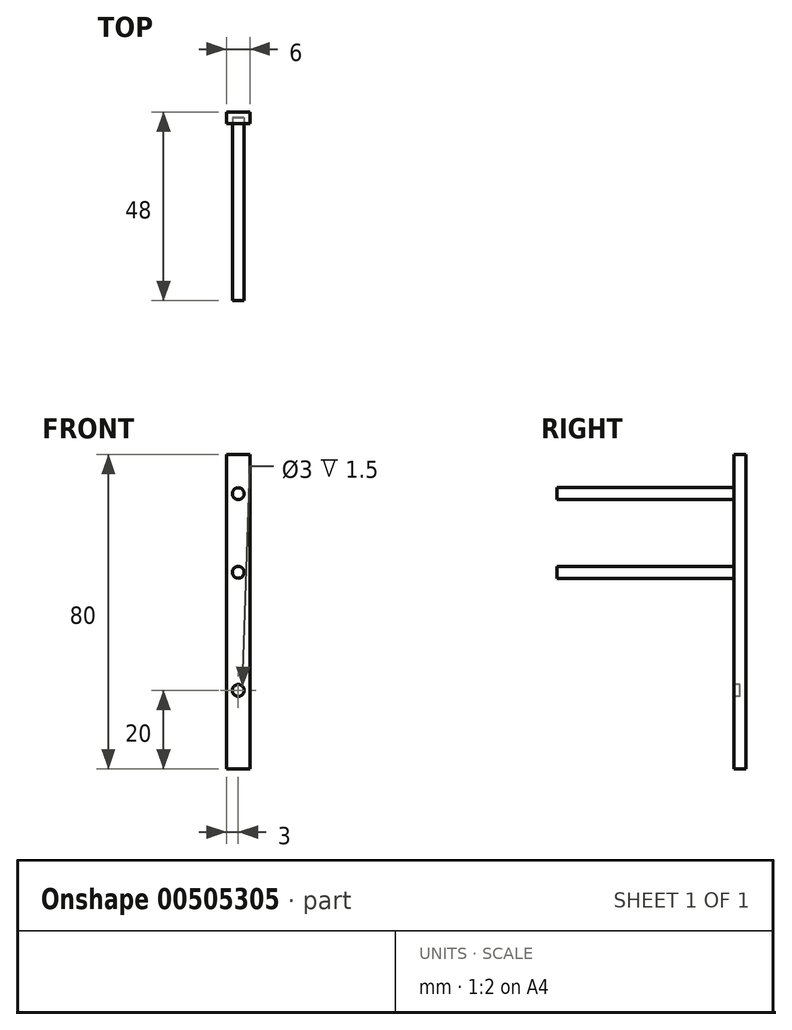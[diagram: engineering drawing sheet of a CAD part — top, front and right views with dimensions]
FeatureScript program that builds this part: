
annotation { "Feature Type Name" : "Feature", "Feature Type Description" : "" }
export const myFeature = defineFeature(function(context is Context, id is Id, definition is map)
    precondition{}
    {
        {
            var Q0;
            Q0=qCreatedBy(makeId("Front.planeOp"),FACE);
            var sketch = newSketch(context, id + "F0", { "sketchPlane" : qUnion([Q0])});
            skLineSegment(sketch, "E0.bottom", {"start": v(3, 40) * mm, "end": v(-3, 40) * mm});
            skLineSegment(sketch, "E0.top", {"start": v(3, -40) * mm, "end": v(-3, -40) * mm});
            skLineSegment(sketch, "E0.left", {"start": v(3, 40) * mm, "end": v(3, -40) * mm});
            skLineSegment(sketch, "E0.right", {"start": v(-3, 40) * mm, "end": v(-3, -40) * mm});
            skPoint(sketch, "E0.middle", {"position": v(0, 0) * mm});
            skSolve(sketch);
        }
        {
            var Q0;
            Q0=makeQuery(id+"F0.imprint","IMPRINT",FACE,{"disambiguationData":[TD([[makeQuery(id+"F0.imprint","IMPRINT",EDGE,{"derivedFrom":sQuery(id+"F0.wireOp",EDGE,"E0.bottom")}),1.0]])]});
            extrude(context, id + "F1", {"entities" : qUnion([Q0]), "depth" : 3 * mm});
        }
        {
            var Q0;
            Q0=makeQuery(id+"F1.opExtrude","CAP_FACE",FACE,{"disambiguationData":[OSD([sQuery(id+"F0.wireOp",EDGE,"E0.bottom"),sQuery(id+"F0.wireOp",EDGE,"E0.top"),sQuery(id+"F0.wireOp",EDGE,"E0.left"),sQuery(id+"F0.wireOp",EDGE,"E0.right")])],"isStart":false});
            var sketch = newSketch(context, id + "F2", { "sketchPlane" : qUnion([Q0])});
            skCircle(sketch, "E1", {"center": v(0, -20) * mm, "radius": 1.5 * mm});
            skSolve(sketch);
        }
        {
            var Q0;
            Q0=makeQuery(id+"F2.imprint","IMPRINT",FACE,{"disambiguationData":[TD([[makeQuery(id+"F2.imprint","IMPRINT",EDGE,{"derivedFrom":sQuery(id+"F2.wireOp",EDGE,"E1")}),1.0]])]});
            extrude(context, id + "F3", {"entities" : qUnion([Q0]), "operationType" : NewBodyOperationType.REMOVE, "oppositeDirection" : true, "depth" : 1.5 * mm});
        }
        {
            var Q0;
            Q0=makeQuery(id+"F1.opExtrude","CAP_FACE",FACE,{"disambiguationData":[OSD([sQuery(id+"F0.wireOp",EDGE,"E0.bottom"),sQuery(id+"F0.wireOp",EDGE,"E0.top"),sQuery(id+"F0.wireOp",EDGE,"E0.left"),sQuery(id+"F0.wireOp",EDGE,"E0.right")])],"isStart":false});
            var sketch = newSketch(context, id + "F4", { "sketchPlane" : qUnion([Q0])});
            skCircle(sketch, "E2", {"center": v(0, 30) * mm, "radius": 1.5 * mm});
            skCircle(sketch, "E3", {"center": v(0, 10) * mm, "radius": 1.5 * mm});
            skSolve(sketch);
        }
        {
            var Q0;
            Q0=makeQuery(id+"F4.imprint","IMPRINT",FACE,{"disambiguationData":[TD([[makeQuery(id+"F4.imprint","IMPRINT",EDGE,{"derivedFrom":sQuery(id+"F4.wireOp",EDGE,"E3")}),1.0]])]});
            var Q1;
            Q1=makeQuery(id+"F4.imprint","IMPRINT",FACE,{"disambiguationData":[TD([[makeQuery(id+"F4.imprint","IMPRINT",EDGE,{"derivedFrom":sQuery(id+"F4.wireOp",EDGE,"E2")}),1.0]])]});
            extrude(context, id + "F5", {"entities" : qUnion([Q0, Q1]), "operationType" : NewBodyOperationType.ADD, "depth" : 45 * mm});
        }
    });
